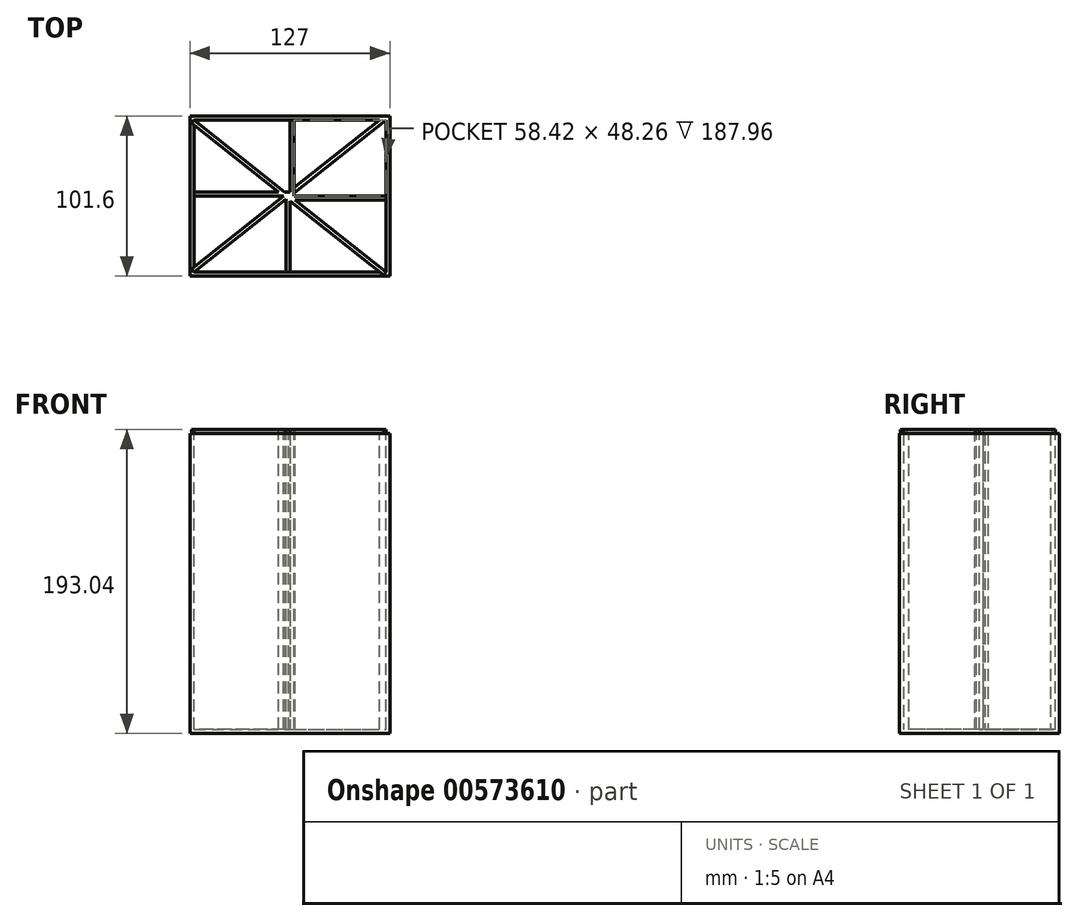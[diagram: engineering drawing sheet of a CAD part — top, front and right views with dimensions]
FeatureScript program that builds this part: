
annotation { "Feature Type Name" : "Feature", "Feature Type Description" : "" }
export const myFeature = defineFeature(function(context is Context, id is Id, definition is map)
    precondition{}
    {
        {
            var Q0;
            Q0=qCreatedBy(makeId("Top.planeOp"),FACE);
            var sketch = newSketch(context, id + "F0", { "sketchPlane" : qUnion([Q0])});
            skLineSegment(sketch, "E0.bottom", {"start": v(-63.5, 50.8) * mm, "end": v(63.5, 50.8) * mm});
            skLineSegment(sketch, "E0.top", {"start": v(-63.5, -50.8) * mm, "end": v(63.5, -50.8) * mm});
            skLineSegment(sketch, "E0.left", {"start": v(-63.5, 50.8) * mm, "end": v(-63.5, -50.8) * mm});
            skLineSegment(sketch, "E0.right", {"start": v(63.5, 50.8) * mm, "end": v(63.5, -50.8) * mm});
            skPoint(sketch, "E0.middle", {"position": v(0, 0) * mm});
            skSolve(sketch);
        }
        {
            var Q0;
            Q0=makeQuery(id+"F0.imprint","IMPRINT",FACE,{"disambiguationData":[TD([[makeQuery(id+"F0.imprint","IMPRINT",EDGE,{"derivedFrom":sQuery(id+"F0.wireOp",EDGE,"E0.bottom")}),-1.0]])]});
            extrude(context, id + "F1", {"entities" : qUnion([Q0]), "depth" : 190.5 * mm, "offsetDistance" : 25.4 * mm});
        }
        {
            var Q0;
            Q0=makeQuery(id+"F1.opExtrude","CAP_FACE",FACE,{"disambiguationData":[OSD([sQuery(id+"F0.wireOp",EDGE,"E0.bottom"),sQuery(id+"F0.wireOp",EDGE,"E0.top"),sQuery(id+"F0.wireOp",EDGE,"E0.left"),sQuery(id+"F0.wireOp",EDGE,"E0.right")])],"isStart":false});
            shell(context, id + "F2", {"entities" : qUnion([Q0]), "thickness" : 2.54 * mm});
        }
        {
            var Q0;
            Q0=makeQuery(id+"F2.opShell","OFFSET_FACE",FACE,{"disambiguationData":[OSD([sQuery(id+"F0.wireOp",EDGE,"E0.bottom"),sQuery(id+"F0.wireOp",EDGE,"E0.top"),sQuery(id+"F0.wireOp",EDGE,"E0.left"),sQuery(id+"F0.wireOp",EDGE,"E0.right")])]});
            var sketch = newSketch(context, id + "F3", { "sketchPlane" : qUnion([Q0])});
            skLineSegment(sketch, "E1", {"start": v(0, 0) * mm, "end": v(60.96, 0) * mm});
            skLineSegment(sketch, "E2", {"start": v(60.96, 0) * mm, "end": v(0, 0) * mm});
            skLineSegment(sketch, "E3", {"start": v(0, 0) * mm, "end": v(0, -48.26) * mm});
            skLineSegment(sketch, "E4", {"start": v(0, -48.26) * mm, "end": v(0, 0) * mm});
            skLineSegment(sketch, "E5", {"start": v(-60.96, 0) * mm, "end": v(0, 0) * mm});
            skLineSegment(sketch, "E6", {"start": v(0, 0) * mm, "end": v(0, 48.26) * mm});
            skLineSegment(sketch, "E7", {"start": v(0, 48.26) * mm, "end": v(0, 0) * mm});
            skLineSegment(sketch, "E8", {"start": v(0, 0) * mm, "end": v(60.96, 48.26) * mm});
            skLineSegment(sketch, "E9", {"start": v(60.96, 48.26) * mm, "end": v(0, 0) * mm});
            skLineSegment(sketch, "E10", {"start": v(0, 0) * mm, "end": v(60.96, -48.26) * mm});
            skLineSegment(sketch, "E11", {"start": v(60.96, -48.26) * mm, "end": v(0, 0) * mm});
            skLineSegment(sketch, "E12", {"start": v(0, 0) * mm, "end": v(-60.96, -48.26) * mm});
            skLineSegment(sketch, "E13", {"start": v(-60.96, -48.26) * mm, "end": v(0, 0) * mm});
            skLineSegment(sketch, "E14", {"start": v(-60.96, 48.26) * mm, "end": v(0, 0) * mm});
            skLineSegment(sketch, "E15", {"start": v(0, 0) * mm, "end": v(-60.96, 48.26) * mm});
            skSolve(sketch);
        }
        {
            var Q0;
            Q0=sQuery(id+"F3.wireOp",EDGE,"E9");
            extrude(context, id + "F4", {"bodyType" : ToolBodyType.SURFACE, "surfaceEntities" : qUnion([Q0]), "depth" : 187.96 * mm, "offsetDistance" : 25.4 * mm});
        }
        {
            var Q0;
            Q0=makeQuery(id+"F2.opShell","OFFSET_FACE",FACE,{"disambiguationData":[OSD([sQuery(id+"F0.wireOp",EDGE,"E0.bottom"),sQuery(id+"F0.wireOp",EDGE,"E0.top"),sQuery(id+"F0.wireOp",EDGE,"E0.left"),sQuery(id+"F0.wireOp",EDGE,"E0.right")])]});
            var sketch = newSketch(context, id + "F5", { "sketchPlane" : qUnion([Q0])});
            skLineSegment(sketch, "E16", {"start": v(0, 0) * mm, "end": v(0, 48.26) * mm});
            skSolve(sketch);
        }
        {
            var Q0;
            Q0=sQuery(id+"F5.wireOp",EDGE,"E16");
            extrude(context, id + "F6", {"bodyType" : ToolBodyType.SURFACE, "surfaceEntities" : qUnion([Q0]), "depth" : 190.5 * mm, "offsetDistance" : 25.4 * mm});
        }
        {
            var Q0;
            Q0=makeQuery(id+"F2.opShell","OFFSET_FACE",FACE,{"disambiguationData":[OSD([sQuery(id+"F0.wireOp",EDGE,"E0.bottom"),sQuery(id+"F0.wireOp",EDGE,"E0.top"),sQuery(id+"F0.wireOp",EDGE,"E0.left"),sQuery(id+"F0.wireOp",EDGE,"E0.right")])]});
            var sketch = newSketch(context, id + "F7", { "sketchPlane" : qUnion([Q0])});
            skLineSegment(sketch, "E17", {"start": v(-60.96, 48.26) * mm, "end": v(0, 0) * mm});
            skSolve(sketch);
        }
        {
            var Q0;
            Q0=sQuery(id+"F7.wireOp",EDGE,"E17");
            extrude(context, id + "F8", {"bodyType" : ToolBodyType.SURFACE, "surfaceEntities" : qUnion([Q0]), "depth" : 190.5 * mm, "offsetDistance" : 25.4 * mm});
        }
        {
            var Q0;
            Q0=makeQuery(id+"F2.opShell","OFFSET_FACE",FACE,{"disambiguationData":[OSD([sQuery(id+"F0.wireOp",EDGE,"E0.bottom"),sQuery(id+"F0.wireOp",EDGE,"E0.top"),sQuery(id+"F0.wireOp",EDGE,"E0.left"),sQuery(id+"F0.wireOp",EDGE,"E0.right")])]});
            var sketch = newSketch(context, id + "F9", { "sketchPlane" : qUnion([Q0])});
            skLineSegment(sketch, "E18", {"start": v(0, 0) * mm, "end": v(-60.96, 0) * mm});
            skSolve(sketch);
        }
        {
            var Q0;
            Q0=sQuery(id+"F9.wireOp",EDGE,"E18");
            extrude(context, id + "F10", {"bodyType" : ToolBodyType.SURFACE, "surfaceEntities" : qUnion([Q0]), "depth" : 190.5 * mm, "offsetDistance" : 25.4 * mm});
        }
        {
            var Q0;
            Q0=makeQuery(id+"F2.opShell","OFFSET_FACE",FACE,{"disambiguationData":[OSD([sQuery(id+"F0.wireOp",EDGE,"E0.bottom"),sQuery(id+"F0.wireOp",EDGE,"E0.top"),sQuery(id+"F0.wireOp",EDGE,"E0.left"),sQuery(id+"F0.wireOp",EDGE,"E0.right")])]});
            var sketch = newSketch(context, id + "F11", { "sketchPlane" : qUnion([Q0])});
            skLineSegment(sketch, "E19", {"start": v(0, 0) * mm, "end": v(-60.96, -48.26) * mm});
            skSolve(sketch);
        }
        {
            var Q0;
            Q0=sQuery(id+"F11.wireOp",EDGE,"E19");
            extrude(context, id + "F12", {"bodyType" : ToolBodyType.SURFACE, "surfaceEntities" : qUnion([Q0]), "depth" : 190.5 * mm, "offsetDistance" : 25.4 * mm});
        }
        {
            var Q0;
            Q0=makeQuery(id+"F2.opShell","OFFSET_FACE",FACE,{"disambiguationData":[OSD([sQuery(id+"F0.wireOp",EDGE,"E0.bottom"),sQuery(id+"F0.wireOp",EDGE,"E0.top"),sQuery(id+"F0.wireOp",EDGE,"E0.left"),sQuery(id+"F0.wireOp",EDGE,"E0.right")])]});
            var sketch = newSketch(context, id + "F13", { "sketchPlane" : qUnion([Q0])});
            skLineSegment(sketch, "E20", {"start": v(0, 0) * mm, "end": v(0, -48.26) * mm});
            skSolve(sketch);
        }
        {
            var Q0;
            Q0=sQuery(id+"F13.wireOp",EDGE,"E20");
            extrude(context, id + "F14", {"bodyType" : ToolBodyType.SURFACE, "surfaceEntities" : qUnion([Q0]), "depth" : 190.5 * mm, "offsetDistance" : 25.4 * mm});
        }
        {
            var Q0;
            Q0=makeQuery(id+"F2.opShell","OFFSET_FACE",FACE,{"disambiguationData":[OSD([sQuery(id+"F0.wireOp",EDGE,"E0.bottom"),sQuery(id+"F0.wireOp",EDGE,"E0.top"),sQuery(id+"F0.wireOp",EDGE,"E0.left"),sQuery(id+"F0.wireOp",EDGE,"E0.right")])]});
            var sketch = newSketch(context, id + "F15", { "sketchPlane" : qUnion([Q0])});
            skLineSegment(sketch, "E21", {"start": v(0, 0) * mm, "end": v(60.96, -48.26) * mm});
            skSolve(sketch);
        }
        {
            var Q0;
            Q0=sQuery(id+"F15.wireOp",EDGE,"E21");
            extrude(context, id + "F16", {"bodyType" : ToolBodyType.SURFACE, "surfaceEntities" : qUnion([Q0]), "depth" : 190.5 * mm, "offsetDistance" : 25.4 * mm});
        }
        {
            var Q0;
            Q0=makeQuery(id+"F2.opShell","OFFSET_FACE",FACE,{"disambiguationData":[OSD([sQuery(id+"F0.wireOp",EDGE,"E0.bottom"),sQuery(id+"F0.wireOp",EDGE,"E0.top"),sQuery(id+"F0.wireOp",EDGE,"E0.left"),sQuery(id+"F0.wireOp",EDGE,"E0.right")])]});
            var sketch = newSketch(context, id + "F17", { "sketchPlane" : qUnion([Q0])});
            skLineSegment(sketch, "E22", {"start": v(0, 0) * mm, "end": v(60.96, 0) * mm});
            skSolve(sketch);
        }
        {
            var Q0;
            Q0=sQuery(id+"F17.wireOp",EDGE,"E22");
            extrude(context, id + "F18", {"bodyType" : ToolBodyType.SURFACE, "surfaceEntities" : qUnion([Q0]), "depth" : 190.5 * mm, "offsetDistance" : 25.4 * mm});
        }
        {
            var Q0;
            Q0=makeQuery(id+"F10.opExtrude","SWEPT_FACE",FACE,{"disambiguationData":[OSD([sQuery(id+"F9.wireOp",EDGE,"E18")])]});
            extrude(context, id + "F19", {"entities" : qUnion([Q0]), "operationType" : NewBodyOperationType.ADD, "depth" : 2.54 * mm, "offsetDistance" : 25.4 * mm});
        }
        {
            var Q0;
            Q0=makeQuery(id+"F12.opExtrude","SWEPT_FACE",FACE,{"disambiguationData":[OSD([sQuery(id+"F11.wireOp",EDGE,"E19")])]});
            extrude(context, id + "F20", {"entities" : qUnion([Q0]), "operationType" : NewBodyOperationType.ADD, "depth" : 2.54 * mm, "offsetDistance" : 25.4 * mm});
        }
        {
            var Q0;
            Q0=makeQuery(id+"F14.opExtrude","SWEPT_FACE",FACE,{"disambiguationData":[OSD([sQuery(id+"F13.wireOp",EDGE,"E20")])]});
            extrude(context, id + "F21", {"entities" : qUnion([Q0]), "operationType" : NewBodyOperationType.ADD, "depth" : 2.54 * mm, "offsetDistance" : 25.4 * mm});
        }
        {
            var Q0;
            Q0=makeQuery(id+"F16.opExtrude","SWEPT_FACE",FACE,{"disambiguationData":[OSD([sQuery(id+"F15.wireOp",EDGE,"E21")])]});
            extrude(context, id + "F22", {"entities" : qUnion([Q0]), "operationType" : NewBodyOperationType.ADD, "depth" : 2.54 * mm, "offsetDistance" : 25.4 * mm});
        }
        {
            var Q0;
            Q0=makeQuery(id+"F18.opExtrude","SWEPT_FACE",FACE,{"disambiguationData":[OSD([sQuery(id+"F17.wireOp",EDGE,"E22")])]});
            extrude(context, id + "F23", {"entities" : qUnion([Q0]), "operationType" : NewBodyOperationType.ADD, "depth" : 2.54 * mm, "offsetDistance" : 25.4 * mm});
        }
        {
            var Q0;
            Q0=makeQuery(id+"F4.opExtrude","SWEPT_FACE",FACE,{"disambiguationData":[OSD([sQuery(id+"F3.wireOp",EDGE,"E9")])]});
            extrude(context, id + "F24", {"entities" : qUnion([Q0]), "operationType" : NewBodyOperationType.ADD, "depth" : 2.54 * mm, "offsetDistance" : 25.4 * mm});
        }
        {
            var Q0;
            Q0=makeQuery(id+"F6.opExtrude","SWEPT_FACE",FACE,{"disambiguationData":[OSD([sQuery(id+"F5.wireOp",EDGE,"E16")])]});
            extrude(context, id + "F25", {"entities" : qUnion([Q0]), "operationType" : NewBodyOperationType.ADD, "depth" : 2.54 * mm, "offsetDistance" : 25.4 * mm});
        }
        {
            var Q0;
            Q0=makeQuery(id+"F8.opExtrude","SWEPT_FACE",FACE,{"disambiguationData":[OSD([sQuery(id+"F7.wireOp",EDGE,"E17")])]});
            extrude(context, id + "F26", {"entities" : qUnion([Q0]), "operationType" : NewBodyOperationType.ADD, "depth" : 2.54 * mm, "offsetDistance" : 25.4 * mm});
        }
    });
